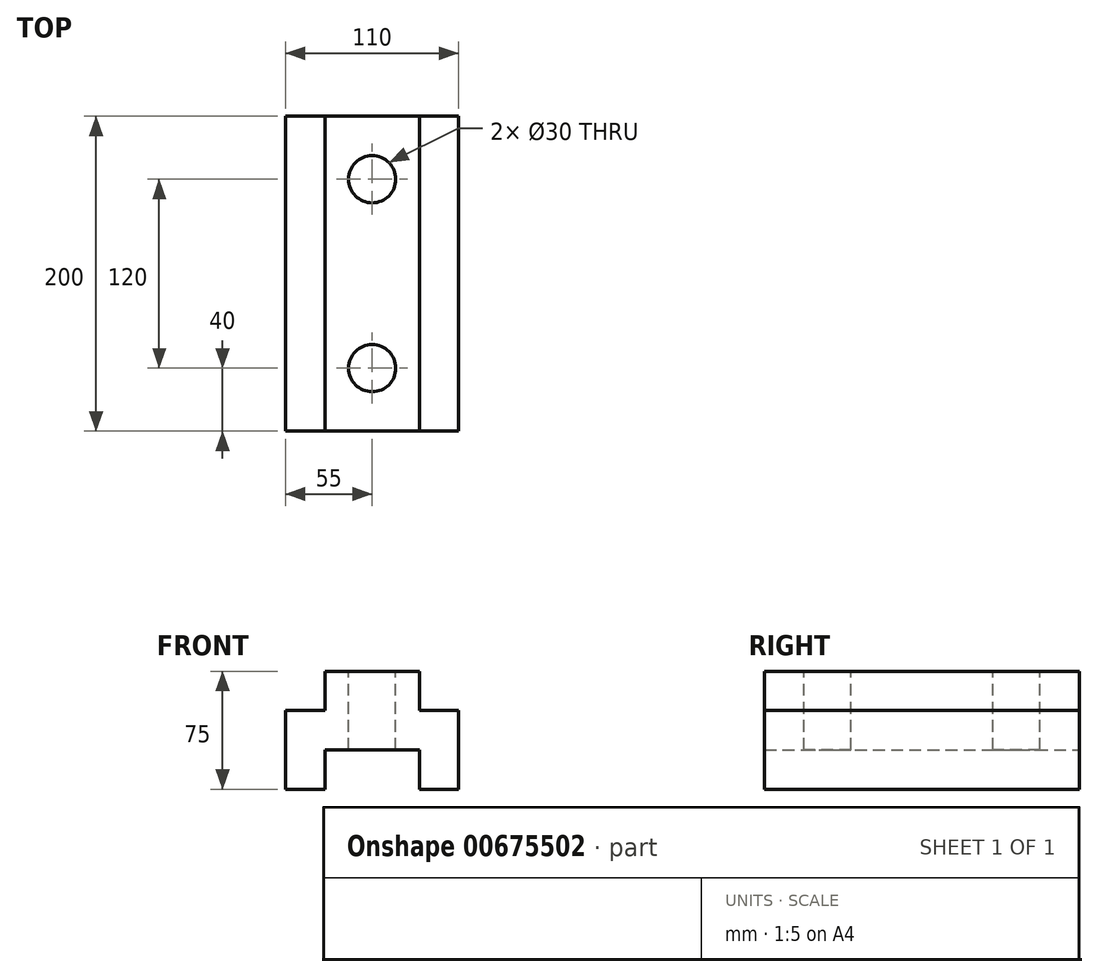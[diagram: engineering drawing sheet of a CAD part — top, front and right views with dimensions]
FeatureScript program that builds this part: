
annotation { "Feature Type Name" : "Feature", "Feature Type Description" : "" }
export const myFeature = defineFeature(function(context is Context, id is Id, definition is map)
    precondition{}
    {
        {
            var Q0;
            Q0=qCreatedBy(makeId("Front.planeOp"),FACE);
            var sketch = newSketch(context, id + "F0", { "sketchPlane" : qUnion([Q0])});
            skLineSegment(sketch, "E0", {"start": v(0, 0) * mm, "end": v(0, 50) * mm});
            skLineSegment(sketch, "E1", {"start": v(0, 50) * mm, "end": v(-25, 50) * mm});
            skLineSegment(sketch, "E2", {"start": v(-25, 50) * mm, "end": v(-25, 75) * mm});
            skLineSegment(sketch, "E3", {"start": v(-25, 75) * mm, "end": v(-85, 75) * mm});
            skLineSegment(sketch, "E4", {"start": v(-85, 75) * mm, "end": v(-85, 50) * mm});
            skLineSegment(sketch, "E5", {"start": v(-85, 50) * mm, "end": v(-110, 50) * mm});
            skLineSegment(sketch, "E6", {"start": v(-110, 50) * mm, "end": v(-110, 0) * mm});
            skLineSegment(sketch, "E7", {"start": v(-110, 0) * mm, "end": v(-85, 0) * mm});
            skLineSegment(sketch, "E8", {"start": v(-85, 0) * mm, "end": v(-85, 25) * mm});
            skLineSegment(sketch, "E9", {"start": v(-85, 25) * mm, "end": v(-25, 25) * mm});
            skLineSegment(sketch, "E10", {"start": v(-25, 25) * mm, "end": v(-25, 0) * mm});
            skLineSegment(sketch, "E11", {"start": v(-25, 0) * mm, "end": v(0, 0) * mm});
            skSolve(sketch);
        }
        {
            var Q0;
            Q0 = qSketchRegion(id + "F0", true);
            extrude(context, id + "F1", {"entities" : qUnion([Q0]), "depth" : 200 * mm, "offsetDistance" : 25 * mm});
        }
        {
            var Q0;
            Q0=makeQuery(id+"F1.opExtrude","SWEPT_FACE",FACE,{"disambiguationData":[OSD([sQuery(id+"F0.wireOp",EDGE,"E3")])]});
            var sketch = newSketch(context, id + "F2", { "sketchPlane" : qUnion([Q0])});
            skCircle(sketch, "E12", {"center": v(-55, -40) * mm, "radius": 15 * mm});
            skPoint(sketch, "E12.centerSnap0", {"position": v(-55, 0) * mm});
            skCircle(sketch, "E13", {"center": v(-55, -160) * mm, "radius": 15 * mm});
            skPoint(sketch, "E13.centerSnap0", {"position": v(-55, -200) * mm});
            skSolve(sketch);
        }
        {
            var Q0;
            Q0 = qSketchRegion(id + "F2", true);
            extrude(context, id + "F3", {"entities" : qUnion([Q0]), "operationType" : NewBodyOperationType.REMOVE, "oppositeDirection" : true, "depth" : 50 * mm, "offsetDistance" : 25 * mm});
        }
    });
